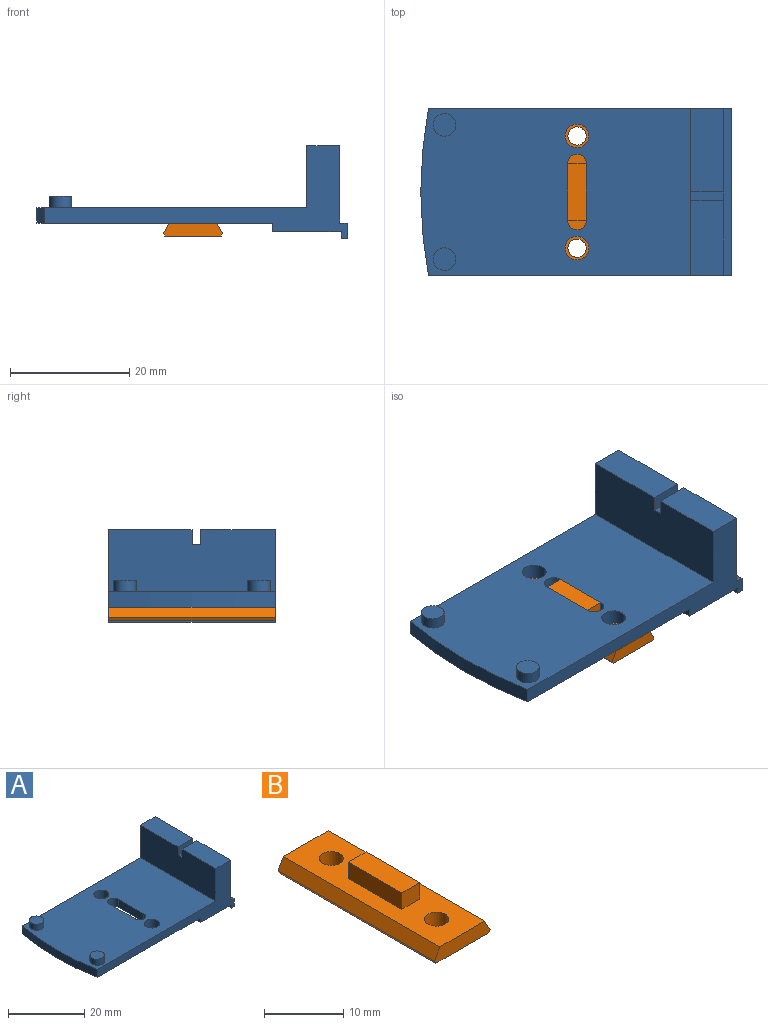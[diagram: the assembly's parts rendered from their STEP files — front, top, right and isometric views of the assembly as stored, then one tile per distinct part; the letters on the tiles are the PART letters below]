
ASSEMBLY  parts=2 mates=2
PART A: 28 faces, bbox 52x27.9x15.5 mm
  f0: plane 27.94x2.57mm, normal (1,0,0), area 71.7mm2, adj f1,f7,f10,f27
  f1: plane 50.7x15.52mm, normal (0,-1,0), area 202.6mm2, adj f0,f2,f3,f4,f5,f6,f8,f9
  f2: plane 39.45x27.94mm, normal (0,0,-1), area 1027.3mm2, adj f1,f7,f8,f11,f12,f13,f23,f24
  f3: plane 45.21x27.94mm, normal (0,0,1), area 1165.9mm2, adj f1,f7,f11,f12,f13,f14,f16,f18
  f4: plane 12.51x5.51mm, normal (0,0,1), area 68.9mm2, adj f1,f5,f18,f20
  f5: plane 27.94x12.95mm, normal (1,0,0), area 358.2mm2, adj f1,f4,f7,f19,f20,f21,f22,f27
  f6: plane 27.94x11.53mm, normal (0,0,-1), area 322.2mm2, adj f1,f7,f8,f9
  f7: plane 50.7x15.52mm, normal (0,1,0), area 202.6mm2, adj f0,f2,f3,f5,f6,f8,f9,f10
  f8: plane 27.94x1.47mm, normal (-1,0,0), area 41.2mm2, adj f1,f2,f6,f7
  f9: plane 27.94x1.09mm, normal (-1,0,0), area 30.5mm2, adj f1,f6,f7,f10
  f10: plane 27.94x1.02mm, normal (0,0,-1), area 28.4mm2, adj f0,f1,f7,f9
  f11: cylinder r=1.98mm len=3.96mm, axis (0,0,1), area 31.6mm2, adj f2,f3
  f12: cylinder r=1.98mm len=3.96mm, axis (0,0,1), area 31.6mm2, adj f2,f3
  f13: cylinder r=76.2mm len=27.94mm, axis (0,0,1), area 71.4mm2, adj f1,f2,f3,f7
  f14: cylinder r=1.89mm len=3.78mm, axis (0,0,-1), area 22.6mm2, adj f3,f15
  f15: plane 3.78x3.78mm, normal (0,0,1), area 11.2mm2, adj f14
  f16: cylinder r=1.89mm len=3.78mm, axis (0,0,-1), area 22.6mm2, adj f3,f17
  f17: plane 3.78x3.78mm, normal (0,0,1), area 11.2mm2, adj f16
  f18: plane 27.94x10.41mm, normal (-1,0,0), area 287.3mm2, adj f1,f3,f4,f7,f19,f20,f21,f22
  f19: plane 13.97x5.51mm, normal (0,0,1), area 77mm2, adj f5,f7,f18,f21
  f20: plane 5.51x2.54mm, normal (0,1,0), area 14mm2, adj f4,f5,f18,f22
  f21: plane 5.51x2.54mm, normal (0,-1,0), area 14mm2, adj f5,f18,f19,f22
  f22: plane 5.51x1.46mm, normal (0,0,1), area 8mm2, adj f5,f18,f20,f21
  f23: cylinder r=1.59mm len=3.18mm, axis (0,0,-1), area 12.7mm2, adj f2,f3,f24,f26
  f24: plane 9.53x2.54mm, normal (1,0,0), area 24.2mm2, adj f2,f3,f23,f25
  f25: cylinder r=1.59mm len=3.18mm, axis (0,0,-1), area 12.7mm2, adj f2,f3,f24,f26
  f26: plane 9.53x2.54mm, normal (-1,0,0), area 24.2mm2, adj f2,f3,f23,f25
  f27: plane 27.94x1.27mm, normal (0,0,1), area 35.5mm2, adj f0,f1,f5,f7
PART B: 15 faces, bbox 9.9x27.9x4.7 mm
  f0: plane 27.94x7.99mm, normal (0,0,1), area 178.5mm2, adj f2,f3,f4,f5,f9,f10,f11,f12
  f1: plane 27.94x9.4mm, normal (0,0,-1), area 248mm2, adj f4,f5,f6,f7,f13,f14
  f2: plane 27.94x1.74mm, normal (0.87,0,0.48), area 55.6mm2, adj f0,f4,f5,f6
  f3: plane 27.94x1.74mm, normal (-0.87,0,0.48), area 55.6mm2, adj f0,f4,f5,f7
  f4: plane 9.92x2.18mm, normal (0,-1,0), area 19.9mm2, adj f0,f1,f2,f3,f6,f7
  f5: plane 9.92x2.18mm, normal (0,1,0), area 19.9mm2, adj f0,f1,f2,f3,f6,f7
  f6: plane 27.94x0.44mm, normal (0.86,0,-0.51), area 14.4mm2, adj f1,f2,f4,f5
  f7: plane 27.94x0.44mm, normal (-0.86,0,-0.51), area 14.4mm2, adj f1,f3,f4,f5
  f8: plane 9.53x3.18mm, normal (0,0,1), area 30.2mm2, adj f9,f10,f11,f12
  f9: plane 9.53x2.54mm, normal (-1,0,0), area 24.2mm2, adj f0,f8,f11,f12
  f10: plane 9.53x2.54mm, normal (1,0,0), area 24.2mm2, adj f0,f8,f11,f12
  f11: plane 3.18x2.54mm, normal (0,-1,0), area 8.1mm2, adj f0,f8,f9,f10
  f12: plane 3.18x2.54mm, normal (0,1,0), area 8.1mm2, adj f0,f8,f9,f10
  f13: cylinder r=1.52mm len=3.05mm, axis (0,0,1), area 20.9mm2, adj f0,f1
  f14: cylinder r=1.52mm len=3.05mm, axis (0,0,1), area 20.9mm2, adj f0,f1
PLACE A t=(2.25,6.27,19.84)mm
PLACE B t=(2.25,6.27,19.84)mm
MATE planar B.f0 <-> A.f2  axis (0,0,1) through (-28.56,6.27,39.93)mm
MATE cylindrical B.f14 <-> A.f12  axis (0,0,1) through (-28.56,-3.13,39.93)mm
